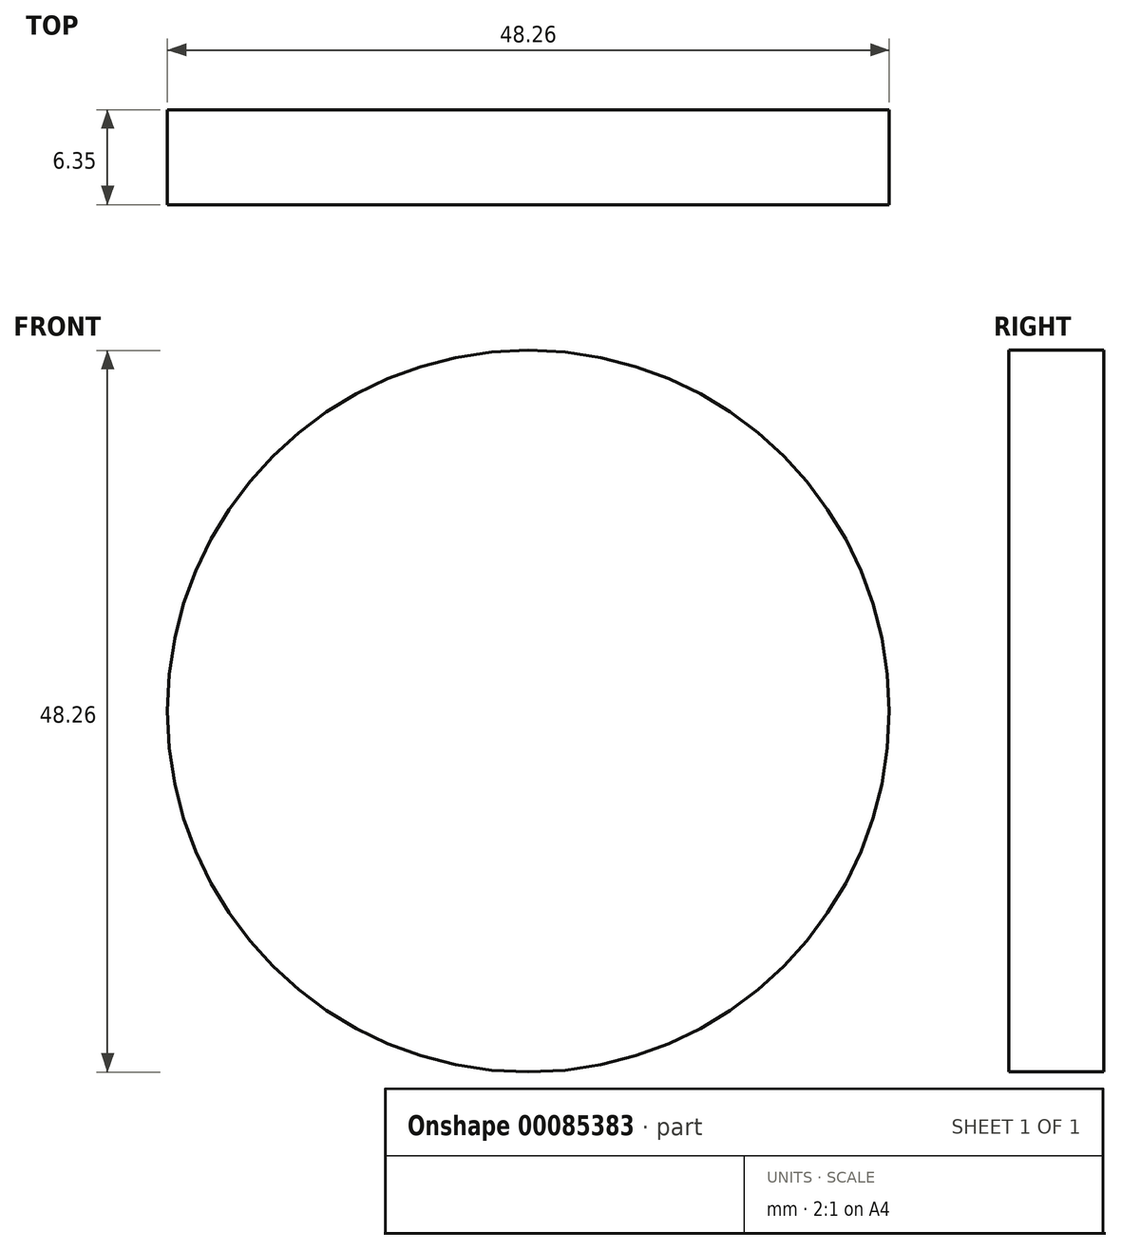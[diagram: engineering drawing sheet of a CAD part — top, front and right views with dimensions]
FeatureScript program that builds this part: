
annotation { "Feature Type Name" : "Feature", "Feature Type Description" : "" }
export const myFeature = defineFeature(function(context is Context, id is Id, definition is map)
    precondition{}
    {
        {
            var Q0;
            Q0=qCreatedBy(makeId("Right.planeOp"),FACE);
            var sketch = newSketch(context, id + "F0", { "sketchPlane" : qUnion([Q0])});
            skLineSegment(sketch, "E0", {"start": v(-131.88, 37.78) * mm, "end": v(-131.88, 6.03) * mm});
            skLineSegment(sketch, "E1", {"start": v(-131.88, 6.03) * mm, "end": v(-30.28, 6.03) * mm});
            skLineSegment(sketch, "E2", {"start": v(-30.28, 6.03) * mm, "end": v(-30.28, 31.43) * mm});
            skFitSpline(sketch, "E3", {"points": [v(-30.28, 31.43) * mm, v(-60.38, 31.43) * mm, v(-111.5, 34.6) * mm, v(-131.88, 37.78) * mm], "startDerivative": vector(-84.62, -5.23) * mm, "endDerivative": vector(-66.06, 9.27) * mm});
            skLineSegment(sketch, "E4.bottom", {"start": v(-131.88, 6.03) * mm, "end": v(-125.53, 6.03) * mm});
            skLineSegment(sketch, "E4.top", {"start": v(-131.88, 30.16) * mm, "end": v(-125.53, 30.16) * mm});
            skLineSegment(sketch, "E4.left", {"start": v(-131.88, 6.03) * mm, "end": v(-131.88, 30.16) * mm});
            skLineSegment(sketch, "E4.right", {"start": v(-125.53, 6.03) * mm, "end": v(-125.53, 30.16) * mm});
            skLineSegment(sketch, "E5.bottom", {"start": v(-125.53, 6.03) * mm, "end": v(-119.18, 6.03) * mm});
            skLineSegment(sketch, "E5.top", {"start": v(-125.53, 27.62) * mm, "end": v(-119.18, 27.62) * mm});
            skLineSegment(sketch, "E5.left", {"start": v(-125.53, 6.03) * mm, "end": v(-125.53, 27.62) * mm});
            skLineSegment(sketch, "E5.right", {"start": v(-119.18, 6.03) * mm, "end": v(-119.18, 27.62) * mm});
            skLineSegment(sketch, "E6.bottom", {"start": v(-30.28, 6.03) * mm, "end": v(-55.68, 6.03) * mm});
            skLineSegment(sketch, "E6.top", {"start": v(-30.28, 18.73) * mm, "end": v(-55.68, 18.73) * mm});
            skLineSegment(sketch, "E6.left", {"start": v(-30.28, 6.03) * mm, "end": v(-30.28, 18.73) * mm});
            skLineSegment(sketch, "E6.right", {"start": v(-55.68, 6.03) * mm, "end": v(-55.68, 18.73) * mm});
            skLineSegment(sketch, "E7", {"start": v(-55.68, 15.56) * mm, "end": v(-119.18, 15.56) * mm});
            skPoint(sketch, "E7.endSnap0", {"position": v(-119.18, 16.83) * mm});
            skSolve(sketch);
        }
        {
            var Q0;
            Q0=makeQuery(id+"F0.imprint","IMPRINT",FACE,{"disambiguationData":[TD([[makeQuery(id+"F0.imprint","IMPRINT",EDGE,{"derivedFrom":sQuery(id+"F0.wireOp",EDGE,"E0")}),1.0]])]});
            var Q1;
            Q1=sQuery(id+"F0.wireOp",EDGE,"E1");
            revolve(context, id + "F1", {"entities" : qUnion([Q0]), "axis" : qUnion([Q1]), "revolveType" : RevolveType.FULL});
        }
    });
